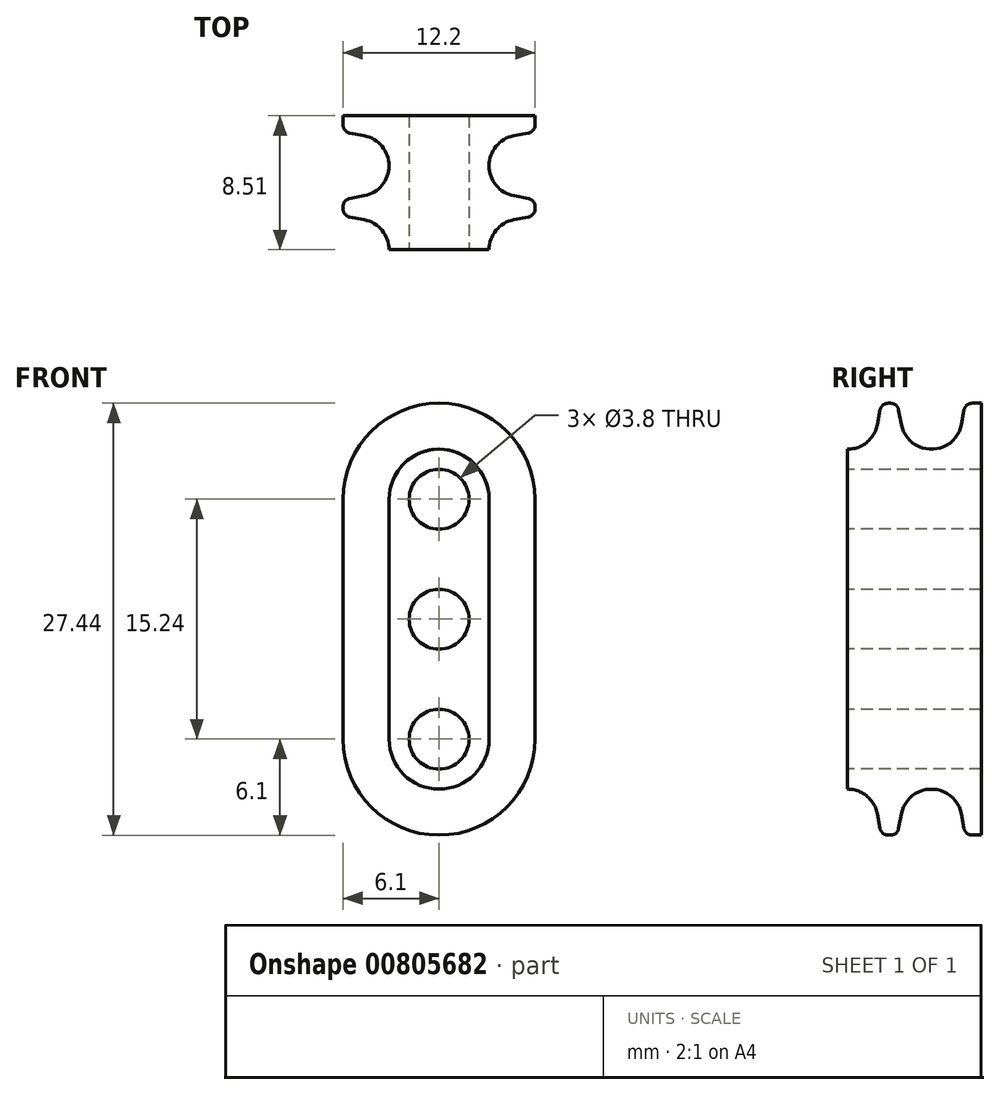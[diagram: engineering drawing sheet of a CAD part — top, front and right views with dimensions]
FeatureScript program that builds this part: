
annotation { "Feature Type Name" : "Feature", "Feature Type Description" : "" }
export const myFeature = defineFeature(function(context is Context, id is Id, definition is map)
    precondition{}
    {
        {
            var Q0;
            Q0=qCreatedBy(makeId("Front.planeOp"),FACE);
            var sketch = newSketch(context, id + "F0", { "sketchPlane" : qUnion([Q0])});
            skCircle(sketch, "E0", {"center": v(0, 0) * mm, "radius": 6.1 * mm});
            skSolve(sketch);
        }
        {
            var Q0;
            Q0=makeQuery(id+"F0.imprint","IMPRINT",FACE,{"disambiguationData":[TD([[makeQuery(id+"F0.imprint","IMPRINT",EDGE,{"derivedFrom":sQuery(id+"F0.wireOp",EDGE,"E0")}),1.0]])]});
            extrude(context, id + "F1", {"entities" : qUnion([Q0]), "depth" : 5.33 * mm, "offsetDistance" : 25.4 * mm, "symmetric" : true});
        }
        {
            var Q0;
            Q0=qCreatedBy(makeId("Front.planeOp"),FACE);
            var sketch = newSketch(context, id + "F2", { "sketchPlane" : qUnion([Q0])});
            skLineSegment(sketch, "E1.bottom", {"start": v(12.6, 0) * mm, "end": v(-13.53, 0) * mm});
            skLineSegment(sketch, "E1.top", {"start": v(12.6, -24.15) * mm, "end": v(-13.53, -24.15) * mm});
            skLineSegment(sketch, "E1.left", {"start": v(12.6, 0) * mm, "end": v(12.6, -24.15) * mm});
            skLineSegment(sketch, "E1.right", {"start": v(-13.53, 0) * mm, "end": v(-13.53, -24.15) * mm});
            skSolve(sketch);
        }
        {
            var Q0;
            Q0=qSketchRegion(id+"F2",true);
            extrude(context, id + "F3", {"entities" : qUnion([Q0]), "operationType" : NewBodyOperationType.REMOVE, "oppositeDirection" : true, "depth" : 12.7 * mm, "offsetDistance" : 25.4 * mm, "symmetric" : true});
        }
        {
            var Q0;
            Q0=makeQuery(id+"F1.opExtrude","CAP_FACE",FACE,{"disambiguationData":[OSD([sQuery(id+"F0.wireOp",EDGE,"E0")])],"isStart":false});
            var sketch = newSketch(context, id + "F4", { "sketchPlane" : qUnion([Q0])});
            skCircle(sketch, "E2", {"center": v(0, 0) * mm, "radius": 1.9 * mm});
            skSolve(sketch);
        }
        {
            var Q0;
            Q0=qCreatedBy(makeId("Right.planeOp"),FACE);
            var sketch = newSketch(context, id + "F5", { "sketchPlane" : qUnion([Q0])});
            skLineSegment(sketch, "E3", {"start": v(2.41, 7.44) * mm, "end": v(1.9, 4.75) * mm});
            skLineSegment(sketch, "E4", {"start": v(-2.41, 7.44) * mm, "end": v(-1.9, 4.75) * mm});
            skLineSegment(sketch, "E5", {"start": v(2.41, 7.44) * mm, "end": v(-2.41, 7.44) * mm});
            skArc(sketch, "E6", {"start": v(-1.9, 4.75) * mm, "mid": v(0, 3.17) * mm, "end": v(1.9, 4.75) * mm});
            skLineSegment(sketch, "E7", {"start": v(11.1, 0) * mm, "end": v(0, 0) * mm, "construction": true});
            skPoint(sketch, "E8", {"position": v(0, 3.18) * mm});
            skLineSegment(sketch, "E9", {"start": v(0, 0) * mm, "end": v(0, 5.11) * mm, "construction": true});
            skLineSegment(sketch, "E10.0", {"start": v(2.67, 0) * mm, "end": v(2.67, 6.1) * mm, "construction": true});
            skPoint(sketch, "E11", {"position": v(2.16, 6.1) * mm});
            skPoint(sketch, "E12", {"position": v(-2.16, 6.1) * mm});
            skLineSegment(sketch, "E13.direction1", {"start": v(-1.9, 4.75) * mm, "end": v(-7.24, 4.75) * mm, "construction": true});
            skLineSegment(sketch, "E14", {"start": v(2.16, 6.1) * mm, "end": v(2.67, 6.1) * mm, "construction": true});
            skLineSegment(sketch, "E15", {"start": v(-2.67, 6.1) * mm, "end": v(-2.16, 6.1) * mm, "construction": true});
            skSolve(sketch);
        }
        {
            var Q0;
            Q0=makeQuery(id+"F5.imprint","IMPRINT",FACE,{"disambiguationData":[TD([[makeQuery(id+"F5.imprint","IMPRINT",EDGE,{"derivedFrom":sQuery(id+"F5.wireOp",EDGE,"E3")}),-1.0]])]});
            var Q1;
            Q1=makeQuery(id+"F5.imprint","IMPRINT",FACE,{"disambiguationData":[TD([[makeQuery(id+"F5.imprint","IMPRINT",EDGE,{"derivedFrom":sQuery(id+"F5.wireOp",EDGE,"E13.1.0.0")}),-1.0]])]});
            var Q2;
            Q2=sQuery(id+"F5.wireOp",EDGE,"E7");
            var Q3;
            Q3=sQuery(id+"F5.wireOp",EDGE,"E7");
            revolve(context, id + "F6", {"operationType" : NewBodyOperationType.REMOVE, "surfaceOperationType" : NewSurfaceOperationType.NEW, "entities" : qUnion([Q0, Q1]), "surfaceEntities" : qUnion([Q2]), "axis" : qUnion([Q3]), "revolveType" : RevolveType.FULL, "oppositeDirection" : true});
        }
        {
            var Q0;
            {var subQ0=sQuery(id+"F2.wireOp",EDGE,"E1.bottom");Q0=makeQuery(id+"FzYgyNMxcEHEfbp_1.boolean.opBoolean","MERGE",FACE,{"derivedFrom":[makeQuery(id+"F3.boolean.opBoolean","COPY",FACE,{"derivedFrom":makeQuery(id+"F3.opExtrude","SWEPT_FACE",FACE,{"disambiguationData":[OSD([subQ0])]})}),makeQuery(id+"FzYgyNMxcEHEfbp_1.opExtrude","SWEPT_FACE",FACE,{"disambiguationData":[OSD([sQuery(id+"F0.wireOp",EDGE,"E0"),subQ0])]})]});}
            extrude(context, id + "F7", {"entities" : qUnion([Q0]), "operationType" : NewBodyOperationType.ADD, "depth" : 7.62 * mm, "offsetDistance" : 25.4 * mm});
        }
        {
            var Q0;
            Q0=makeQuery(id+"F1.opExtrude","SWEPT_BODY",BODY,{"disambiguationData":[OSD([sQuery(id+"F0.wireOp",EDGE,"E0")])]});
            var Q1;
            Q1=makeQuery(id+"F7.opExtrude","CAP_FACE",FACE,{"disambiguationData":[OSD([sQuery(id+"F0.wireOp",EDGE,"E0"),sQuery(id+"F2.wireOp",EDGE,"E1.bottom")])],"isStart":false});
            mirror(context, id + "F8", {"operationType" : NewBodyOperationType.ADD, "entities" : qUnion([Q0]), "mirrorPlane" : qUnion([Q1])});
        }
        {
            var Q0;
            Q0=makeQuery(id+"F1.opExtrude","SWEPT_BODY",BODY,{"disambiguationData":[OSD([sQuery(id+"F0.wireOp",EDGE,"E0")])]});
            var Q1;
            {var subQ0=sQuery(id+"F2.wireOp",EDGE,"E1.bottom");var subQ1=sQuery(id+"F0.wireOp",EDGE,"E0");var subQ2=makeQuery(id+"F1.opExtrude","CAP_FACE",FACE,{"disambiguationData":[OSD([subQ1])],"isStart":false});var subQ3=makeQuery(id+"F7.boolean.opBoolean","MERGE",FACE,{"derivedFrom":[subQ2,makeQuery(id+"F7.opExtrude","SWEPT_FACE",FACE,{"disambiguationData":[OSD([subQ1,subQ0]),TDD([makeQuery(id+"F3.boolean.opBoolean","INTERSECT",EDGE,{"derivedFrom":[subQ2,makeQuery(id+"F3.opExtrude","SWEPT_FACE",FACE,{"disambiguationData":[OSD([subQ0])]})]})])]})]});Q1=makeQuery(id+"F8.boolean.opBoolean","MERGE",FACE,{"derivedFrom":[subQ3,makeQuery(id+"F8.opPattern","COPY",FACE,{"derivedFrom":subQ3,"instanceName":"1"})]});}
            mirror(context, id + "F9", {"operationType" : NewBodyOperationType.ADD, "entities" : qUnion([Q0]), "mirrorPlane" : qUnion([Q1])});
        }
        {
            var Q0;
            Q0=qCreatedBy(makeId("Right.planeOp"),FACE);
            var sketch = newSketch(context, id + "F10", { "sketchPlane" : qUnion([Q0])});
            skLineSegment(sketch, "E16.bottom", {"start": v(-5.33, 7.62) * mm, "end": v(-15.12, 7.62) * mm});
            skLineSegment(sketch, "E16.top", {"start": v(-5.33, -23.05) * mm, "end": v(-15.12, -23.05) * mm});
            skLineSegment(sketch, "E16.left", {"start": v(-5.33, 7.62) * mm, "end": v(-5.33, -23.05) * mm});
            skLineSegment(sketch, "E16.right", {"start": v(-15.12, 7.62) * mm, "end": v(-15.12, -23.05) * mm});
            skSolve(sketch);
        }
        {
            var Q0;
            Q0=qSketchRegion(id+"F10",true);
            extrude(context, id + "F11", {"entities" : qUnion([Q0]), "operationType" : NewBodyOperationType.REMOVE, "oppositeDirection" : true, "depth" : 25.4 * mm, "offsetDistance" : 25.4 * mm, "symmetric" : true});
        }
        {
            var Q0;
            Q0=makeQuery(id+"F1.opExtrude","SWEPT_BODY",BODY,{"disambiguationData":[OSD([sQuery(id+"F0.wireOp",EDGE,"E0")])]});
            var Q1;
            Q1=makeQuery(id+"F11.boolean.opBoolean","COPY",FACE,{"derivedFrom":makeQuery(id+"F11.opExtrude","SWEPT_FACE",FACE,{"disambiguationData":[OSD([sQuery(id+"F10.wireOp",EDGE,"E16.left")])]})});
            mirror(context, id + "F12", {"operationType" : NewBodyOperationType.ADD, "entities" : qUnion([Q0]), "mirrorPlane" : qUnion([Q1])});
        }
        {
            var Q0;
            Q0=qSketchRegion(id+"F4",true);
            extrude(context, id + "F13", {"entities" : qUnion([Q0]), "operationType" : NewBodyOperationType.REMOVE, "oppositeDirection" : true, "depth" : 127 * mm, "offsetDistance" : 25.4 * mm, "symmetric" : true});
        }
        {
            var Q0;
            {var subQ0=sQuery(id+"F2.wireOp",EDGE,"E1.bottom");var subQ1=sQuery(id+"F0.wireOp",EDGE,"E0");var subQ2=makeQuery(id+"F1.opExtrude","CAP_FACE",FACE,{"disambiguationData":[OSD([subQ1])],"isStart":true});var subQ3=makeQuery(id+"F7.boolean.opBoolean","MERGE",FACE,{"derivedFrom":[subQ2,makeQuery(id+"F7.opExtrude","SWEPT_FACE",FACE,{"disambiguationData":[OSD([subQ1,subQ0]),TDD([makeQuery(id+"F3.boolean.opBoolean","INTERSECT",EDGE,{"derivedFrom":[subQ2,makeQuery(id+"F3.opExtrude","SWEPT_FACE",FACE,{"disambiguationData":[OSD([subQ0])]})]})])]})]});Q0=makeQuery(id+"F8.boolean.opBoolean","MERGE",FACE,{"derivedFrom":[subQ3,makeQuery(id+"F8.opPattern","COPY",FACE,{"derivedFrom":subQ3,"instanceName":"1"})]});}
            extrude(context, id + "F14", {"entities" : qUnion([Q0]), "operationType" : NewBodyOperationType.ADD, "depth" : 0.5 * mm, "offsetDistance" : 25.4 * mm});
        }
        {
            var Q0;
            Q0=qCreatedBy(makeId("Front.planeOp"),FACE);
            var sketch = newSketch(context, id + "F15", { "sketchPlane" : qUnion([Q0])});
            skCircle(sketch, "E17.0", {"center": v(0, 0) * mm, "radius": 1.9 * mm});
            skCircle(sketch, "E18.0.1.0", {"center": v(0, -7.62) * mm, "radius": 1.9 * mm});
            skCircle(sketch, "E18.0.2.0", {"center": v(0, -15.24) * mm, "radius": 1.9 * mm});
            skLineSegment(sketch, "E18.direction1", {"start": v(0, 0) * mm, "end": v(25.4, 0) * mm, "construction": true});
            skLineSegment(sketch, "E18.direction2", {"start": v(0, 0) * mm, "end": v(0, -7.62) * mm, "construction": true});
            skSolve(sketch);
        }
        {
            var Q0;
            Q0=qSketchRegion(id+"F15",true);
            var Q1;
            Q1=sQuery(id+"F15.wireOp",EDGE,"E18.0.1.0");
            var Q2;
            Q2=sQuery(id+"F15.wireOp",EDGE,"E18.0.2.0");
            extrude(context, id + "F16", {"entities" : qUnion([Q0]), "operationType" : NewBodyOperationType.REMOVE, "surfaceEntities" : qUnion([Q1, Q2]), "oppositeDirection" : true, "depth" : 127 * mm, "offsetDistance" : 25.4 * mm, "symmetric" : true});
        }
        {
            var Q0;
            {var subQ0=sQuery(id+"F0.wireOp",EDGE,"E0");Q0=makeQuery(id+"F6.boolean.opBoolean","INTERSECT",EDGE,{"derivedFrom":[makeQuery(id+"FzYgyNMxcEHEfbp_1.boolean.opBoolean","MERGE",FACE,{"derivedFrom":[makeQuery(id+"F1.opExtrude","SWEPT_FACE",FACE,{"disambiguationData":[OSD([subQ0])]}),makeQuery(id+"FzYgyNMxcEHEfbp_1.opExtrude","SWEPT_FACE",FACE,{"disambiguationData":[OSD([subQ0])]})]}),makeQuery(id+"F6.opRevolve","SWEPT_FACE",FACE,{"disambiguationData":[OSD([sQuery(id+"F5.wireOp",EDGE,"E4")])]})]});}
            var Q1;
            {var subQ0=sQuery(id+"F0.wireOp",EDGE,"E0");Q1=makeQuery(id+"F6.boolean.opBoolean","INTERSECT",EDGE,{"derivedFrom":[makeQuery(id+"FzYgyNMxcEHEfbp_1.boolean.opBoolean","MERGE",FACE,{"derivedFrom":[makeQuery(id+"F1.opExtrude","SWEPT_FACE",FACE,{"disambiguationData":[OSD([subQ0])]}),makeQuery(id+"FzYgyNMxcEHEfbp_1.opExtrude","SWEPT_FACE",FACE,{"disambiguationData":[OSD([subQ0])]})]}),makeQuery(id+"F6.opRevolve","SWEPT_FACE",FACE,{"disambiguationData":[OSD([sQuery(id+"F5.wireOp",EDGE,"E3")])]})]});}
            var Q2;
            Q2=makeQuery(id+"F9.opPattern","COPY",EDGE,{"derivedFrom":makeQuery(id+"F6.boolean.opBoolean","INTERSECT",EDGE,{"derivedFrom":[makeQuery(id+"F1.opExtrude","SWEPT_FACE",FACE,{"disambiguationData":[OSD([sQuery(id+"F0.wireOp",EDGE,"E0")])]}),makeQuery(id+"F6.opRevolve","SWEPT_FACE",FACE,{"disambiguationData":[OSD([sQuery(id+"F5.wireOp",EDGE,"E4")])]})]}),"instanceName":"1"});
            var Q3;
            Q3=makeQuery(id+"F12.opPattern","COPY",EDGE,{"derivedFrom":makeQuery(id+"F9.opPattern","COPY",EDGE,{"derivedFrom":makeQuery(id+"F6.boolean.opBoolean","INTERSECT",EDGE,{"derivedFrom":[makeQuery(id+"F1.opExtrude","SWEPT_FACE",FACE,{"disambiguationData":[OSD([sQuery(id+"F0.wireOp",EDGE,"E0")])]}),makeQuery(id+"F6.opRevolve","SWEPT_FACE",FACE,{"disambiguationData":[OSD([sQuery(id+"F5.wireOp",EDGE,"E4")])]})]}),"instanceName":"1"}),"instanceName":"1"});
            fillet(context, id + "F17", {"entities" : qUnion([Q0, Q1, Q2, Q3]), "radius" : 0.5 * mm, "tangentPropagation" : true, "allowEdgeOverflow" : false});
        }
        {
            var Q0;
            Q0=qCreatedBy(makeId("Right.planeOp"),FACE);
            var sketch = newSketch(context, id + "F18", { "sketchPlane" : qUnion([Q0])});
            skLineSegment(sketch, "E19.bottom", {"start": v(-18.16, 9.74) * mm, "end": v(-10.67, 9.74) * mm});
            skLineSegment(sketch, "E19.top", {"start": v(-18.16, -24.18) * mm, "end": v(-10.67, -24.18) * mm});
            skLineSegment(sketch, "E19.left", {"start": v(-18.16, 9.74) * mm, "end": v(-18.16, -24.18) * mm});
            skLineSegment(sketch, "E19.right", {"start": v(-10.67, 9.74) * mm, "end": v(-10.67, -24.18) * mm});
            skSolve(sketch);
        }
        {
            var Q0;
            Q0=qSketchRegion(id+"F18",true);
            extrude(context, id + "F19", {"entities" : qUnion([Q0]), "operationType" : NewBodyOperationType.REMOVE, "depth" : 25.4 * mm, "offsetDistance" : 25.4 * mm, "symmetric" : true});
        }
        {
            var Q0;
            Q0=qCreatedBy(makeId("Right.planeOp"),FACE);
            var sketch = newSketch(context, id + "F20", { "sketchPlane" : qUnion([Q0])});
            skLineSegment(sketch, "E20.bottom", {"start": v(-14.22, 8.6) * mm, "end": v(-5.33, 8.6) * mm});
            skLineSegment(sketch, "E20.top", {"start": v(-14.22, -24.57) * mm, "end": v(-5.33, -24.57) * mm});
            skLineSegment(sketch, "E20.left", {"start": v(-14.22, 8.6) * mm, "end": v(-14.22, -24.57) * mm});
            skLineSegment(sketch, "E20.right", {"start": v(-5.33, 8.6) * mm, "end": v(-5.33, -24.57) * mm});
            skSolve(sketch);
        }
        {
            var Q0;
            Q0 = qSketchRegion(id + "F20", true);
            extrude(context, id + "F21", {"entities" : qUnion([Q0]), "operationType" : NewBodyOperationType.REMOVE, "oppositeDirection" : true, "depth" : 25.4 * mm, "offsetDistance" : 25.4 * mm, "symmetric" : true});
        }
    });
